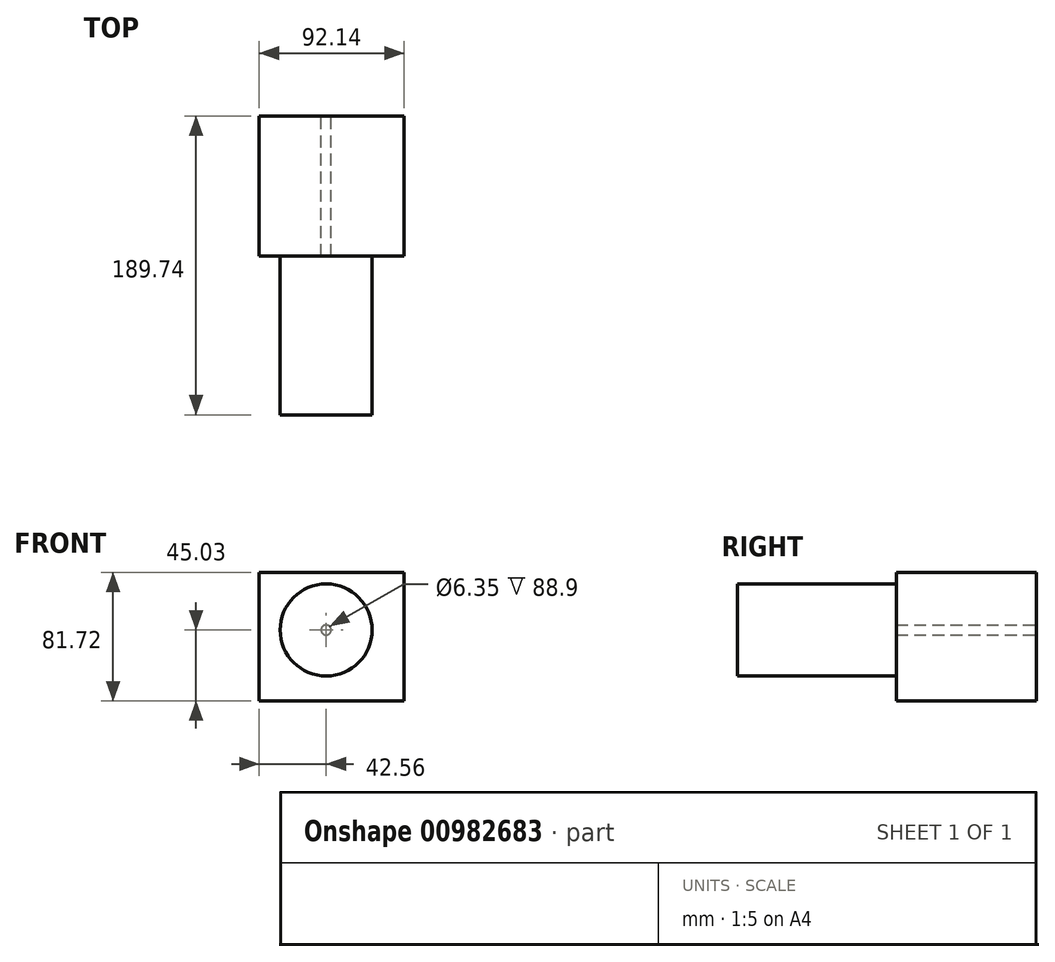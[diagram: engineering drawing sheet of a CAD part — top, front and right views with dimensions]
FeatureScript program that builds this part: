
annotation { "Feature Type Name" : "Feature", "Feature Type Description" : "" }
export const myFeature = defineFeature(function(context is Context, id is Id, definition is map)
    precondition{}
    {
        {
            var Q0;
            Q0=qCreatedBy(makeId("Front.planeOp"),FACE);
            var sketch = newSketch(context, id + "F0", { "sketchPlane" : qUnion([Q0])});
            skLineSegment(sketch, "E0.bottom", {"start": v(-42.56, 36.69) * mm, "end": v(49.58, 36.69) * mm});
            skLineSegment(sketch, "E0.top", {"start": v(-42.56, -45.03) * mm, "end": v(49.58, -45.03) * mm});
            skLineSegment(sketch, "E0.left", {"start": v(-42.56, 36.69) * mm, "end": v(-42.56, -45.03) * mm});
            skLineSegment(sketch, "E0.right", {"start": v(49.58, 36.69) * mm, "end": v(49.58, -45.03) * mm});
            skSolve(sketch);
        }
        {
            var Q0;
            Q0=makeQuery(id+"F0.imprint","IMPRINT",FACE,{"disambiguationData":[TD([[makeQuery(id+"F0.imprint","IMPRINT",EDGE,{"derivedFrom":sQuery(id+"F0.wireOp",EDGE,"E0.bottom")}),-1.0]])]});
            extrude(context, id + "F1", {"entities" : qUnion([Q0]), "depth" : 88.9 * mm, "offsetDistance" : 25.4 * mm});
        }
        {
            var Q0;
            Q0=makeQuery(id+"F1.opExtrude","CAP_FACE",FACE,{"disambiguationData":[OSD([sQuery(id+"F0.wireOp",EDGE,"E0.bottom"),sQuery(id+"F0.wireOp",EDGE,"E0.top"),sQuery(id+"F0.wireOp",EDGE,"E0.left"),sQuery(id+"F0.wireOp",EDGE,"E0.right")])],"isStart":false});
            var sketch = newSketch(context, id + "F2", { "sketchPlane" : qUnion([Q0])});
            skCircle(sketch, "E1", {"center": v(0, 0) * mm, "radius": 11.23 * mm});
            skSolve(sketch);
        }
        {
            var Q0;
            Q0=sQuery(id+"F2.wireOp",VERTEX,"E1.center");
            var Q1;
            Q1=makeQuery(id+"F1.opExtrude","SWEPT_BODY",BODY,{"disambiguationData":[OSD([sQuery(id+"F0.wireOp",EDGE,"E0.bottom"),sQuery(id+"F0.wireOp",EDGE,"E0.top"),sQuery(id+"F0.wireOp",EDGE,"E0.left"),sQuery(id+"F0.wireOp",EDGE,"E0.right")])]});
            hole(context, id + "F3", {"style" : HoleStyle.SIMPLE, "endStyle" : HoleEndStyle.THROUGH, "holeDiameter" : 6.35 * mm, "majorDiameter" : 6.35 * mm, "isTappedThrough" : true, "tappedDepth" : 12.7 * mm, "tapClearance" : 3, "locations" : qUnion([Q0]), "scope" : qUnion([Q1]), "startStyle" : HoleStartStyle.PART});
        }
        {
            var Q0;
            Q0=makeQuery(id+"F1.opExtrude","CAP_FACE",FACE,{"disambiguationData":[OSD([sQuery(id+"F0.wireOp",EDGE,"E0.bottom"),sQuery(id+"F0.wireOp",EDGE,"E0.top"),sQuery(id+"F0.wireOp",EDGE,"E0.left"),sQuery(id+"F0.wireOp",EDGE,"E0.right")])],"isStart":false});
            var sketch = newSketch(context, id + "F4", { "sketchPlane" : qUnion([Q0])});
            skCircle(sketch, "E2", {"center": v(0, 0) * mm, "radius": 29.22 * mm});
            skSolve(sketch);
        }
        {
            var Q0;
            Q0 = qSketchRegion(id + "F4", true);
            extrude(context, id + "F5", {"entities" : qUnion([Q0]), "operationType" : NewBodyOperationType.ADD, "depth" : 100.84 * mm, "offsetDistance" : 25.4 * mm});
        }
    });
